# Revit family: ВИРС-М фланцевый DN15-200, PN25
name_source: partatom
category: Арматура трубопроводов
revit_build: Autodesk Revit 2015 (Build: 20140322_1515(x64)
units: mm (PartAtom-declared; Revit-internal decimal feet)

## types (88) — shared parameters
URL = http://vogez.by
Видимость клапана = Да
Диаметр подключение провода = 15 мм
Диаметр штока = 30 мм
Длина привода = 115 мм
Длина присоединения провода = 15 мм
Изготовитель = ООО "ВОГЕЗЭНЕРГО"
Интерфес (основной) = RS 232
Исполнение PN = 2
Материал и цвет ППР = Сталь, белый
Материал и цвет остальных элементов = Сталь, неокрашенная
Материал и цвет привода ППР = Пластик, серый
Наименование = Счётчик-расходомер электромагнитный
Номинальное давление PN = 2.5 МПа
Расстояние до провода = 30 мм
Скругления привода = 20 мм
Ширина привода = 65 мм

## per-type parameters (varying)
- Счётчик-расходомер электромагнитный (фланцевый) ВИРС-М DN15, PN25, серия 1000: DN=15 мм; Высота основания привода=80 мм; Высота с приводом=120 мм; Выходной сигнал=числоимпульсный; Диаметр зеркала=51 мм; Диаметр зеркала_2=21 мм; Диаметр корпуса=60 мм; Диаметр патрубка=35 мм; Диаметр условный DN=15 мм; Диаметр фланца=100 мм; Длина корпуса=72 мм; Длина по фланцам=120 мм; Исполнение=1; Класс точности=2; Максимальная температура среды=150 °C; Максимальный расход=5.0 м³/ч; Масса=3.10 kg; Минимальный расход=0.0 м³/ч; Обозначение=ВИРС-М-15-Ф-25-55-232-1000-200; Потребляемая мощность=5 Вт; Радиус условный=8 мм; Радиус фланца=50 мм; Серия=1000; Степень защиты=IP55; Строительная высота=170 мм; Строительная длина=150 мм; Тип, марка=ВИРС-М-15-Ф-25-55-232-1000-200; Толщина зеркала=2 мм; Толщина фланца=12 мм
- Счётчик-расходомер электромагнитный (фланцевый) ВИРС-М DN15, PN25, серия 2000: DN=15 мм; Высота основания привода=80 мм; Высота с приводом=120 мм; Выходной сигнал=числоимпульсный; Диаметр зеркала=51 мм; Диаметр зеркала_2=21 мм; Диаметр корпуса=60 мм; Диаметр патрубка=35 мм; Диаметр условный DN=15 мм; Диаметр фланца=100 мм; Длина корпуса=72 мм; Длина по фланцам=120 мм; Исполнение=2; Класс точности=2; Максимальная температура среды=150 °C; Максимальный расход=6.3 м³/ч; Масса=3.10 kg; Минимальный расход=0.0 м³/ч; Обозначение=ВИРС-М-15-Ф-25-55-232-2000-200; Потребляемая мощность=5 Вт; Радиус условный=8 мм; Радиус фланца=50 мм; Серия=2000; Степень защиты=IP55; Строительная высота=170 мм; Строительная длина=150 мм; Тип, марка=ВИРС-М-15-Ф-25-55-232-2000-200; Толщина зеркала=2 мм; Толщина фланца=12 мм
- Счётчик-расходомер электромагнитный (фланцевый) ВИРС-М DN15, PN25, серия 1100: DN=15 мм; Высота основания привода=80 мм; Высота с приводом=120 мм; Выходной сигнал=числоимпульсный; Диаметр зеркала=51 мм; Диаметр зеркала_2=21 мм; Диаметр корпуса=60 мм; Диаметр патрубка=35 мм; Диаметр условный DN=15 мм; Диаметр фланца=100 мм; Длина корпуса=72 мм; Длина по фланцам=120 мм; Исполнение=3; Класс точности=1; Максимальная температура среды=150 °C; Максимальный расход=5.0 м³/ч; Масса=3.10 kg; Минимальный расход=0.0 м³/ч; Обозначение=ВИРС-М-15-Ф-25-55-232-1100-100; Потребляемая мощность=5 Вт; Радиус условный=8 мм; Радиус фланца=50 мм; Серия=1100; Степень защиты=IP55; Строительная высота=170 мм; Строительная длина=150 мм; Тип, марка=ВИРС-М-15-Ф-25-55-232-1100-100; Толщина зеркала=2 мм; Толщина фланца=12 мм
- Счётчик-расходомер электромагнитный (фланцевый) ВИРС-М DN15, PN25, серия 2100: DN=15 мм; Высота основания привода=80 мм; Высота с приводом=120 мм; Выходной сигнал=числоимпульсный; Диаметр зеркала=51 мм; Диаметр зеркала_2=21 мм; Диаметр корпуса=60 мм; Диаметр патрубка=35 мм; Диаметр условный DN=15 мм; Диаметр фланца=100 мм; Длина корпуса=72 мм; Длина по фланцам=120 мм; Исполнение=4; Класс точности=1; Максимальная температура среды=150 °C; Максимальный расход=6.3 м³/ч; Масса=3.10 kg; Минимальный расход=0.0 м³/ч; Обозначение=ВИРС-М-15-Ф-25-55-232-2100-100; Потребляемая мощность=5 Вт; Радиус условный=8 мм; Радиус фланца=50 мм; Серия=2100; Степень защиты=IP55; Строительная высота=170 мм; Строительная длина=150 мм; Тип, марка=ВИРС-М-15-Ф-25-55-232-2100-100; Толщина зеркала=2 мм; Толщина фланца=12 мм
- Счётчик-расходомер электромагнитный (фланцевый) ВИРС-М DN15, PN25, серия 1300: DN=15 мм; Высота основания привода=80 мм; Высота с приводом=120 мм; Выходной сигнал=частотный; Диаметр зеркала=51 мм; Диаметр зеркала_2=21 мм; Диаметр корпуса=60 мм; Диаметр патрубка=35 мм; Диаметр условный DN=15 мм; Диаметр фланца=100 мм; Длина корпуса=72 мм; Длина по фланцам=120 мм; Исполнение=5; Класс точности=0.5; Максимальная температура среды=90 °C; Максимальный расход=5.0 м³/ч; Масса=3.10 kg; Минимальный расход=0.1 м³/ч; Обозначение=ВИРС-М-15-Ф-25-57-232-1300-050; Потребляемая мощность=5 Вт; Радиус условный=8 мм; Радиус фланца=50 мм; Серия=1300; Степень защиты=IP57; Строительная высота=170 мм; Строительная длина=150 мм; Тип, марка=ВИРС-М-15-Ф-25-57-232-1300-050; Толщина зеркала=2 мм; Толщина фланца=12 мм
- Счётчик-расходомер электромагнитный (фланцевый) ВИРС-М DN15, PN25, серия 2300: DN=15 мм; Высота основания привода=80 мм; Высота с приводом=120 мм; Выходной сигнал=частотный; Диаметр зеркала=51 мм; Диаметр зеркала_2=21 мм; Диаметр корпуса=60 мм; Диаметр патрубка=35 мм; Диаметр условный DN=15 мм; Диаметр фланца=100 мм; Длина корпуса=72 мм; Длина по фланцам=120 мм; Исполнение=6; Класс точности=0.5; Максимальная температура среды=90 °C; Максимальный расход=6.3 м³/ч; Масса=3.10 kg; Минимальный расход=0.1 м³/ч; Обозначение=ВИРС-М-15-Ф-25-57-232-2300-050; Потребляемая мощность=5 Вт; Радиус условный=8 мм; Радиус фланца=50 мм; Серия=2300; Степень защиты=IP57; Строительная высота=170 мм; Строительная длина=150 мм; Тип, марка=ВИРС-М-15-Ф-25-57-232-2300-050; Толщина зеркала=2 мм; Толщина фланца=12 мм
- Счётчик-расходомер электромагнитный (фланцевый) ВИРС-М DN15, PN25, серия 1500: DN=15 мм; Высота основания привода=80 мм; Высота с приводом=120 мм; Выходной сигнал=частотный; Диаметр зеркала=51 мм; Диаметр зеркала_2=21 мм; Диаметр корпуса=60 мм; Диаметр патрубка=35 мм; Диаметр условный DN=15 мм; Диаметр фланца=100 мм; Длина корпуса=72 мм; Длина по фланцам=120 мм; Исполнение=7; Класс точности=0.25; Максимальная температура среды=90 °C; Максимальный расход=5.0 м³/ч; Масса=3.10 kg; Минимальный расход=0.2 м³/ч; Обозначение=ВИРС-М-15-Ф-25-57-232-1500-025; Потребляемая мощность=7 Вт; Радиус условный=8 мм; Радиус фланца=50 мм; Серия=1500; Степень защиты=IP57; Строительная высота=170 мм; Строительная длина=150 мм; Тип, марка=ВИРС-М-15-Ф-25-57-232-1500-025; Толщина зеркала=2 мм; Толщина фланца=12 мм
- Счётчик-расходомер электромагнитный (фланцевый) ВИРС-М DN15, PN25, серия 2500: DN=15 мм; Высота основания привода=80 мм; Высота с приводом=120 мм; Выходной сигнал=частотный; Диаметр зеркала=51 мм; Диаметр зеркала_2=21 мм; Диаметр корпуса=60 мм; Диаметр патрубка=35 мм; Диаметр условный DN=15 мм; Диаметр фланца=100 мм; Длина корпуса=72 мм; Длина по фланцам=120 мм; Исполнение=8; Класс точности=0.25; Максимальная температура среды=90 °C; Максимальный расход=6.3 м³/ч; Масса=3.10 kg; Минимальный расход=0.3 м³/ч; Обозначение=ВИРС-М-15-Ф-25-57-232-2500-025; Потребляемая мощность=7 Вт; Радиус условный=8 мм; Радиус фланца=50 мм; Серия=2500; Степень защиты=IP57; Строительная высота=170 мм; Строительная длина=150 мм; Тип, марка=ВИРС-М-15-Ф-25-57-232-2500-025; Толщина зеркала=2 мм; Толщина фланца=12 мм
- Счётчик-расходомер электромагнитный (фланцевый) ВИРС-М DN20, PN25, серия 1000: DN=20 мм; Высота основания привода=85 мм; Высота с приводом=125 мм; Выходной сигнал=числоимпульсный; Диаметр зеркала=60 мм; Диаметр зеркала_2=25 мм; Диаметр корпуса=70 мм; Диаметр патрубка=40 мм; Диаметр условный DN=20 мм; Диаметр фланца=110 мм; Длина корпуса=68 мм; Длина по фланцам=120 мм; Исполнение=1; Класс точности=2; Максимальная температура среды=150 °C; Максимальный расход=7.9 м³/ч; Масса=3.20 kg; Минимальный расход=0.0 м³/ч; Обозначение=ВИРС-М-20-Ф-25-55-232-1000-200; Потребляемая мощность=5 Вт; Радиус условный=10 мм; Радиус фланца=55 мм; Серия=1000; Степень защиты=IP55; Строительная высота=180 мм; Строительная длина=150 мм; Тип, марка=ВИРС-М-20-Ф-25-55-232-1000-200; Толщина зеркала=2 мм; Толщина фланца=14 мм
- Счётчик-расходомер электромагнитный (фланцевый) ВИРС-М DN20, PN25, серия 1100: DN=20 мм; Высота основания привода=85 мм; Высота с приводом=125 мм; Выходной сигнал=числоимпульсный; Диаметр зеркала=60 мм; Диаметр зеркала_2=25 мм; Диаметр корпуса=70 мм; Диаметр патрубка=40 мм; Диаметр условный DN=20 мм; Диаметр фланца=110 мм; Длина корпуса=68 мм; Длина по фланцам=120 мм; Исполнение=3; Класс точности=1; Максимальная температура среды=150 °C; Максимальный расход=7.9 м³/ч; Масса=3.20 kg; Минимальный расход=0.0 м³/ч; Обозначение=ВИРС-М-20-Ф-25-55-232-1100-100; Потребляемая мощность=5 Вт; Радиус условный=10 мм; Радиус фланца=55 мм; Серия=1100; Степень защиты=IP55; Строительная высота=180 мм; Строительная длина=150 мм; Тип, марка=ВИРС-М-20-Ф-25-55-232-1100-100; Толщина зеркала=2 мм; Толщина фланца=14 мм
- Счётчик-расходомер электромагнитный (фланцевый) ВИРС-М DN20, PN25, серия 1300: DN=20 мм; Высота основания привода=85 мм; Высота с приводом=125 мм; Выходной сигнал=частотный; Диаметр зеркала=60 мм; Диаметр зеркала_2=25 мм; Диаметр корпуса=70 мм; Диаметр патрубка=40 мм; Диаметр условный DN=20 мм; Диаметр фланца=110 мм; Длина корпуса=68 мм; Длина по фланцам=120 мм; Исполнение=5; Класс точности=0.5; Максимальная температура среды=90 °C; Максимальный расход=7.9 м³/ч; Масса=3.20 kg; Минимальный расход=0.1 м³/ч; Обозначение=ВИРС-М-20-Ф-25-57-232-1300-050; Потребляемая мощность=5 Вт; Радиус условный=10 мм; Радиус фланца=55 мм; Серия=1300; Степень защиты=IP57; Строительная высота=180 мм; Строительная длина=150 мм; Тип, марка=ВИРС-М-20-Ф-25-57-232-1300-050; Толщина зеркала=2 мм; Толщина фланца=14 мм
- Счётчик-расходомер электромагнитный (фланцевый) ВИРС-М DN20, PN25, серия 1500: DN=20 мм; Высота основания привода=85 мм; Высота с приводом=125 мм; Выходной сигнал=частотный; Диаметр зеркала=60 мм; Диаметр зеркала_2=25 мм; Диаметр корпуса=70 мм; Диаметр патрубка=40 мм; Диаметр условный DN=20 мм; Диаметр фланца=110 мм; Длина корпуса=68 мм; Длина по фланцам=120 мм; Исполнение=7; Класс точности=0.25; Максимальная температура среды=90 °C; Максимальный расход=7.9 м³/ч; Масса=3.20 kg; Минимальный расход=0.3 м³/ч; Обозначение=ВИРС-М-20-Ф-25-57-232-1500-025; Потребляемая мощность=7 Вт; Радиус условный=10 мм; Радиус фланца=55 мм; Серия=1500; Степень защиты=IP57; Строительная высота=180 мм; Строительная длина=150 мм; Тип, марка=ВИРС-М-20-Ф-25-57-232-1500-025; Толщина зеркала=2 мм; Толщина фланца=14 мм
- Счётчик-расходомер электромагнитный (фланцевый) ВИРС-М DN20, PN25, серия 2000: DN=20 мм; Высота основания привода=85 мм; Высота с приводом=125 мм; Выходной сигнал=числоимпульсный; Диаметр зеркала=60 мм; Диаметр зеркала_2=25 мм; Диаметр корпуса=70 мм; Диаметр патрубка=40 мм; Диаметр условный DN=20 мм; Диаметр фланца=110 мм; Длина корпуса=68 мм; Длина по фланцам=120 мм; Исполнение=2; Класс точности=2; Максимальная температура среды=150 °C; Максимальный расход=10.0 м³/ч; Масса=3.20 kg; Минимальный расход=0.0 м³/ч; Обозначение=ВИРС-М-20-Ф-25-55-232-2000-200; Потребляемая мощность=5 Вт; Радиус условный=10 мм; Радиус фланца=55 мм; Серия=2000; Степень защиты=IP55; Строительная высота=180 мм; Строительная длина=150 мм; Тип, марка=ВИРС-М-20-Ф-25-55-232-2000-200; Толщина зеркала=2 мм; Толщина фланца=14 мм
- Счётчик-расходомер электромагнитный (фланцевый) ВИРС-М DN20, PN25, серия 2100: DN=20 мм; Высота основания привода=85 мм; Высота с приводом=125 мм; Выходной сигнал=числоимпульсный; Диаметр зеркала=60 мм; Диаметр зеркала_2=25 мм; Диаметр корпуса=70 мм; Диаметр патрубка=40 мм; Диаметр условный DN=20 мм; Диаметр фланца=110 мм; Длина корпуса=68 мм; Длина по фланцам=120 мм; Исполнение=4; Класс точности=1; Максимальная температура среды=150 °C; Максимальный расход=10.0 м³/ч; Масса=3.20 kg; Минимальный расход=0.0 м³/ч; Обозначение=ВИРС-М-20-Ф-25-55-232-2100-100; Потребляемая мощность=5 Вт; Радиус условный=10 мм; Радиус фланца=55 мм; Серия=2100; Степень защиты=IP55; Строительная высота=180 мм; Строительная длина=150 мм; Тип, марка=ВИРС-М-20-Ф-25-55-232-2100-100; Толщина зеркала=2 мм; Толщина фланца=14 мм
- Счётчик-расходомер электромагнитный (фланцевый) ВИРС-М DN20, PN25, серия 2300: DN=20 мм; Высота основания привода=85 мм; Высота с приводом=125 мм; Выходной сигнал=частотный; Диаметр зеркала=60 мм; Диаметр зеркала_2=25 мм; Диаметр корпуса=70 мм; Диаметр патрубка=40 мм; Диаметр условный DN=20 мм; Диаметр фланца=110 мм; Длина корпуса=68 мм; Длина по фланцам=120 мм; Исполнение=6; Класс точности=0.5; Максимальная температура среды=90 °C; Максимальный расход=10.0 м³/ч; Масса=3.20 kg; Минимальный расход=0.1 м³/ч; Обозначение=ВИРС-М-20-Ф-25-57-232-2300-050; Потребляемая мощность=5 Вт; Радиус условный=10 мм; Радиус фланца=55 мм; Серия=2300; Степень защиты=IP57; Строительная высота=180 мм; Строительная длина=150 мм; Тип, марка=ВИРС-М-20-Ф-25-57-232-2300-050; Толщина зеркала=2 мм; Толщина фланца=14 мм
- Счётчик-расходомер электромагнитный (фланцевый) ВИРС-М DN20, PN25, серия 2500: DN=20 мм; Высота основания привода=85 мм; Высота с приводом=125 мм; Выходной сигнал=частотный; Диаметр зеркала=60 мм; Диаметр зеркала_2=25 мм; Диаметр корпуса=70 мм; Диаметр патрубка=40 мм; Диаметр условный DN=20 мм; Диаметр фланца=110 мм; Длина корпуса=68 мм; Длина по фланцам=120 мм; Исполнение=8; Класс точности=0.25; Максимальная температура среды=90 °C; Максимальный расход=10.0 м³/ч; Масса=3.20 kg; Минимальный расход=0.4 м³/ч; Обозначение=ВИРС-М-20-Ф-25-57-232-2500-025; Потребляемая мощность=7 Вт; Радиус условный=10 мм; Радиус фланца=55 мм; Серия=2500; Степень защиты=IP57; Строительная высота=180 мм; Строительная длина=150 мм; Тип, марка=ВИРС-М-20-Ф-25-57-232-2500-025; Толщина зеркала=2 мм; Толщина фланца=14 мм
- Счётчик-расходомер электромагнитный (фланцевый) ВИРС-М DN25, PN25, серия 1000: DN=25 мм; Высота основания привода=90 мм; Высота с приводом=130 мм; Выходной сигнал=числоимпульсный; Диаметр зеркала=71 мм; Диаметр зеркала_2=31 мм; Диаметр корпуса=80 мм; Диаметр патрубка=45 мм; Диаметр условный DN=25 мм; Диаметр фланца=120 мм; Длина корпуса=64 мм; Длина по фланцам=120 мм; Исполнение=1; Класс точности=2; Максимальная температура среды=150 °C; Максимальный расход=12.5 м³/ч; Масса=3.60 kg; Минимальный расход=0.0 м³/ч; Обозначение=ВИРС-М-25-Ф-25-55-232-1000-200; Потребляемая мощность=5 Вт; Радиус условный=13 мм; Радиус фланца=60 мм; Серия=1000; Степень защиты=IP55; Строительная высота=190 мм; Строительная длина=150 мм; Тип, марка=ВИРС-М-25-Ф-25-55-232-1000-200; Толщина зеркала=2 мм; Толщина фланца=16 мм
- Счётчик-расходомер электромагнитный (фланцевый) ВИРС-М DN25, PN25, серия 1100: DN=25 мм; Высота основания привода=90 мм; Высота с приводом=130 мм; Выходной сигнал=числоимпульсный; Диаметр зеркала=71 мм; Диаметр зеркала_2=31 мм; Диаметр корпуса=80 мм; Диаметр патрубка=45 мм; Диаметр условный DN=25 мм; Диаметр фланца=120 мм; Длина корпуса=64 мм; Длина по фланцам=120 мм; Исполнение=3; Класс точности=1; Максимальная температура среды=150 °C; Максимальный расход=12.5 м³/ч; Масса=3.60 kg; Минимальный расход=0.1 м³/ч; Обозначение=ВИРС-М-25-Ф-25-55-232-1100-100; Потребляемая мощность=5 Вт; Радиус условный=13 мм; Радиус фланца=60 мм; Серия=1100; Степень защиты=IP55; Строительная высота=190 мм; Строительная длина=150 мм; Тип, марка=ВИРС-М-25-Ф-25-55-232-1100-100; Толщина зеркала=2 мм; Толщина фланца=16 мм
- Счётчик-расходомер электромагнитный (фланцевый) ВИРС-М DN25, PN25, серия 1300: DN=25 мм; Высота основания привода=90 мм; Высота с приводом=130 мм; Выходной сигнал=частотный; Диаметр зеркала=71 мм; Диаметр зеркала_2=31 мм; Диаметр корпуса=80 мм; Диаметр патрубка=45 мм; Диаметр условный DN=25 мм; Диаметр фланца=120 мм; Длина корпуса=64 мм; Длина по фланцам=120 мм; Исполнение=5; Класс точности=0.5; Максимальная температура среды=90 °C; Максимальный расход=12.5 м³/ч; Масса=3.60 kg; Минимальный расход=0.1 м³/ч; Обозначение=ВИРС-М-25-Ф-25-57-232-1300-050; Потребляемая мощность=5 Вт; Радиус условный=13 мм; Радиус фланца=60 мм; Серия=1300; Степень защиты=IP57; Строительная высота=190 мм; Строительная длина=150 мм; Тип, марка=ВИРС-М-25-Ф-25-57-232-1300-050; Толщина зеркала=2 мм; Толщина фланца=16 мм
- Счётчик-расходомер электромагнитный (фланцевый) ВИРС-М DN25, PN25, серия 1500: DN=25 мм; Высота основания привода=90 мм; Высота с приводом=130 мм; Выходной сигнал=частотный; Диаметр зеркала=71 мм; Диаметр зеркала_2=31 мм; Диаметр корпуса=80 мм; Диаметр патрубка=45 мм; Диаметр условный DN=25 мм; Диаметр фланца=120 мм; Длина корпуса=64 мм; Длина по фланцам=120 мм; Исполнение=7; Класс точности=0.25; Максимальная температура среды=90 °C; Максимальный расход=12.5 м³/ч; Масса=3.60 kg; Минимальный расход=0.5 м³/ч; Обозначение=ВИРС-М-25-Ф-25-57-232-1500-025; Потребляемая мощность=7 Вт; Радиус условный=13 мм; Радиус фланца=60 мм; Серия=1500; Степень защиты=IP57; Строительная высота=190 мм; Строительная длина=150 мм; Тип, марка=ВИРС-М-25-Ф-25-57-232-1500-025; Толщина зеркала=2 мм; Толщина фланца=16 мм
- Счётчик-расходомер электромагнитный (фланцевый) ВИРС-М DN25, PN25, серия 2000: DN=25 мм; Высота основания привода=90 мм; Высота с приводом=130 мм; Выходной сигнал=числоимпульсный; Диаметр зеркала=71 мм; Диаметр зеркала_2=31 мм; Диаметр корпуса=80 мм; Диаметр патрубка=45 мм; Диаметр условный DN=25 мм; Диаметр фланца=120 мм; Длина корпуса=64 мм; Длина по фланцам=120 мм; Исполнение=2; Класс точности=2; Максимальная температура среды=150 °C; Максимальный расход=16.0 м³/ч; Масса=3.60 kg; Минимальный расход=0.0 м³/ч; Обозначение=ВИРС-М-25-Ф-25-55-232-2000-200; Потребляемая мощность=5 Вт; Радиус условный=13 мм; Радиус фланца=60 мм; Серия=2000; Степень защиты=IP55; Строительная высота=190 мм; Строительная длина=150 мм; Тип, марка=ВИРС-М-25-Ф-25-55-232-2000-200; Толщина зеркала=2 мм; Толщина фланца=16 мм
- Счётчик-расходомер электромагнитный (фланцевый) ВИРС-М DN25, PN25, серия 2100: DN=25 мм; Высота основания привода=90 мм; Высота с приводом=130 мм; Выходной сигнал=числоимпульсный; Диаметр зеркала=71 мм; Диаметр зеркала_2=31 мм; Диаметр корпуса=80 мм; Диаметр патрубка=45 мм; Диаметр условный DN=25 мм; Диаметр фланца=120 мм; Длина корпуса=64 мм; Длина по фланцам=120 мм; Исполнение=4; Класс точности=1; Максимальная температура среды=150 °C; Максимальный расход=16.0 м³/ч; Масса=3.60 kg; Минимальный расход=0.1 м³/ч; Обозначение=ВИРС-М-25-Ф-25-55-232-2100-100; Потребляемая мощность=5 Вт; Радиус условный=13 мм; Радиус фланца=60 мм; Серия=2100; Степень защиты=IP55; Строительная высота=190 мм; Строительная длина=150 мм; Тип, марка=ВИРС-М-25-Ф-25-55-232-2100-100; Толщина зеркала=2 мм; Толщина фланца=16 мм
- Счётчик-расходомер электромагнитный (фланцевый) ВИРС-М DN25, PN25, серия 2300: DN=25 мм; Высота основания привода=90 мм; Высота с приводом=130 мм; Выходной сигнал=частотный; Диаметр зеркала=71 мм; Диаметр зеркала_2=31 мм; Диаметр корпуса=80 мм; Диаметр патрубка=45 мм; Диаметр условный DN=25 мм; Диаметр фланца=120 мм; Длина корпуса=64 мм; Длина по фланцам=120 мм; Исполнение=6; Класс точности=0.5; Максимальная температура среды=90 °C; Максимальный расход=16.0 м³/ч; Масса=3.60 kg; Минимальный расход=0.2 м³/ч; Обозначение=ВИРС-М-25-Ф-25-57-232-2300-050; Потребляемая мощность=5 Вт; Радиус условный=13 мм; Радиус фланца=60 мм; Серия=2300; Степень защиты=IP57; Строительная высота=190 мм; Строительная длина=150 мм; Тип, марка=ВИРС-М-25-Ф-25-57-232-2300-050; Толщина зеркала=2 мм; Толщина фланца=16 мм
- Счётчик-расходомер электромагнитный (фланцевый) ВИРС-М DN25, PN25, серия 2500: DN=25 мм; Высота основания привода=90 мм; Высота с приводом=130 мм; Выходной сигнал=частотный; Диаметр зеркала=71 мм; Диаметр зеркала_2=31 мм; Диаметр корпуса=80 мм; Диаметр патрубка=45 мм; Диаметр условный DN=25 мм; Диаметр фланца=120 мм; Длина корпуса=64 мм; Длина по фланцам=120 мм; Исполнение=8; Класс точности=0.25; Максимальная температура среды=90 °C; Максимальный расход=16.0 м³/ч; Масса=3.60 kg; Минимальный расход=0.6 м³/ч; Обозначение=ВИРС-М-25-Ф-25-57-232-2500-025; Потребляемая мощность=7 Вт; Радиус условный=13 мм; Радиус фланца=60 мм; Серия=2500; Степень защиты=IP57; Строительная высота=190 мм; Строительная длина=150 мм; Тип, марка=ВИРС-М-25-Ф-25-57-232-2500-025; Толщина зеркала=2 мм; Толщина фланца=16 мм
- Счётчик-расходомер электромагнитный (фланцевый) ВИРС-М DN32, PN25, серия 1000: DN=32 мм; Высота основания привода=103 мм; Высота с приводом=143 мм; Выходной сигнал=числоимпульсный; Диаметр зеркала=82 мм; Диаметр зеркала_2=36 мм; Диаметр корпуса=95 мм; Диаметр патрубка=52 мм; Диаметр условный DN=32 мм; Диаметр фланца=135 мм; Длина корпуса=114 мм; Длина по фланцам=170 мм; Исполнение=1; Класс точности=2; Максимальная температура среды=150 °C; Максимальный расход=20.0 м³/ч; Масса=4.20 kg; Минимальный расход=0.0 м³/ч; Обозначение=ВИРС-М-32-Ф-25-55-232-1000-200; Потребляемая мощность=5 Вт; Радиус условный=16 мм; Радиус фланца=68 мм; Серия=1000; Степень защиты=IP55; Строительная высота=210 мм; Строительная длина=200 мм; Тип, марка=ВИРС-М-32-Ф-25-55-232-1000-200; Толщина зеркала=2 мм; Толщина фланца=16 мм
- Счётчик-расходомер электромагнитный (фланцевый) ВИРС-М DN32, PN25, серия 1100: DN=32 мм; Высота основания привода=103 мм; Высота с приводом=143 мм; Выходной сигнал=числоимпульсный; Диаметр зеркала=82 мм; Диаметр зеркала_2=36 мм; Диаметр корпуса=95 мм; Диаметр патрубка=52 мм; Диаметр условный DN=32 мм; Диаметр фланца=135 мм; Длина корпуса=114 мм; Длина по фланцам=170 мм; Исполнение=3; Класс точности=1; Максимальная температура среды=150 °C; Максимальный расход=20.0 м³/ч; Масса=4.20 kg; Минимальный расход=0.1 м³/ч; Обозначение=ВИРС-М-32-Ф-25-55-232-1100-100; Потребляемая мощность=5 Вт; Радиус условный=16 мм; Радиус фланца=68 мм; Серия=1100; Степень защиты=IP55; Строительная высота=210 мм; Строительная длина=200 мм; Тип, марка=ВИРС-М-32-Ф-25-55-232-1100-100; Толщина зеркала=2 мм; Толщина фланца=16 мм
- Счётчик-расходомер электромагнитный (фланцевый) ВИРС-М DN32, PN25, серия 1300: DN=32 мм; Высота основания привода=103 мм; Высота с приводом=143 мм; Выходной сигнал=частотный; Диаметр зеркала=82 мм; Диаметр зеркала_2=36 мм; Диаметр корпуса=95 мм; Диаметр патрубка=52 мм; Диаметр условный DN=32 мм; Диаметр фланца=135 мм; Длина корпуса=114 мм; Длина по фланцам=170 мм; Исполнение=5; Класс точности=0.5; Максимальная температура среды=90 °C; Максимальный расход=20.0 м³/ч; Масса=4.20 kg; Минимальный расход=0.2 м³/ч; Обозначение=ВИРС-М-32-Ф-25-57-232-1300-050; Потребляемая мощность=5 Вт; Радиус условный=16 мм; Радиус фланца=68 мм; Серия=1300; Степень защиты=IP57; Строительная высота=210 мм; Строительная длина=200 мм; Тип, марка=ВИРС-М-32-Ф-25-57-232-1300-050; Толщина зеркала=2 мм; Толщина фланца=16 мм
- Счётчик-расходомер электромагнитный (фланцевый) ВИРС-М DN32, PN25, серия 1500: DN=32 мм; Высота основания привода=103 мм; Высота с приводом=143 мм; Выходной сигнал=частотный; Диаметр зеркала=82 мм; Диаметр зеркала_2=36 мм; Диаметр корпуса=95 мм; Диаметр патрубка=52 мм; Диаметр условный DN=32 мм; Диаметр фланца=135 мм; Длина корпуса=114 мм; Длина по фланцам=170 мм; Исполнение=7; Класс точности=0.25; Максимальная температура среды=90 °C; Максимальный расход=20.0 м³/ч; Масса=4.20 kg; Минимальный расход=0.8 м³/ч; Обозначение=ВИРС-М-32-Ф-25-57-232-1500-025; Потребляемая мощность=7 Вт; Радиус условный=16 мм; Радиус фланца=68 мм; Серия=1500; Степень защиты=IP57; Строительная высота=210 мм; Строительная длина=200 мм; Тип, марка=ВИРС-М-32-Ф-25-57-232-1500-025; Толщина зеркала=2 мм; Толщина фланца=16 мм
- Счётчик-расходомер электромагнитный (фланцевый) ВИРС-М DN32, PN25, серия 2000: DN=32 мм; Высота основания привода=103 мм; Высота с приводом=143 мм; Выходной сигнал=числоимпульсный; Диаметр зеркала=82 мм; Диаметр зеркала_2=36 мм; Диаметр корпуса=95 мм; Диаметр патрубка=52 мм; Диаметр условный DN=32 мм; Диаметр фланца=135 мм; Длина корпуса=114 мм; Длина по фланцам=170 мм; Исполнение=2; Класс точности=2; Максимальная температура среды=150 °C; Максимальный расход=25.0 м³/ч; Масса=4.20 kg; Минимальный расход=0.1 м³/ч; Обозначение=ВИРС-М-32-Ф-25-55-232-2000-200; Потребляемая мощность=5 Вт; Радиус условный=16 мм; Радиус фланца=68 мм; Серия=2000; Степень защиты=IP55; Строительная высота=210 мм; Строительная длина=200 мм; Тип, марка=ВИРС-М-32-Ф-25-55-232-2000-200; Толщина зеркала=2 мм; Толщина фланца=16 мм
- Счётчик-расходомер электромагнитный (фланцевый) ВИРС-М DN32, PN25, серия 2100: DN=32 мм; Высота основания привода=103 мм; Высота с приводом=143 мм; Выходной сигнал=числоимпульсный; Диаметр зеркала=82 мм; Диаметр зеркала_2=36 мм; Диаметр корпуса=95 мм; Диаметр патрубка=52 мм; Диаметр условный DN=32 мм; Диаметр фланца=135 мм; Длина корпуса=114 мм; Длина по фланцам=170 мм; Исполнение=4; Класс точности=1; Максимальная температура среды=150 °C; Максимальный расход=25.0 м³/ч; Масса=4.20 kg; Минимальный расход=0.1 м³/ч; Обозначение=ВИРС-М-32-Ф-25-55-232-2100-100; Потребляемая мощность=5 Вт; Радиус условный=16 мм; Радиус фланца=68 мм; Серия=2100; Степень защиты=IP55; Строительная высота=210 мм; Строительная длина=200 мм; Тип, марка=ВИРС-М-32-Ф-25-55-232-2100-100; Толщина зеркала=2 мм; Толщина фланца=16 мм
- Счётчик-расходомер электромагнитный (фланцевый) ВИРС-М DN32, PN25, серия 2300: DN=32 мм; Высота основания привода=103 мм; Высота с приводом=143 мм; Выходной сигнал=частотный; Диаметр зеркала=82 мм; Диаметр зеркала_2=36 мм; Диаметр корпуса=95 мм; Диаметр патрубка=52 мм; Диаметр условный DN=32 мм; Диаметр фланца=135 мм; Длина корпуса=114 мм; Длина по фланцам=170 мм; Исполнение=6; Класс точности=0.5; Максимальная температура среды=90 °C; Максимальный расход=25.0 м³/ч; Масса=4.20 kg; Минимальный расход=0.3 м³/ч; Обозначение=ВИРС-М-32-Ф-25-57-232-2300-050; Потребляемая мощность=5 Вт; Радиус условный=16 мм; Радиус фланца=68 мм; Серия=2300; Степень защиты=IP57; Строительная высота=210 мм; Строительная длина=200 мм; Тип, марка=ВИРС-М-32-Ф-25-57-232-2300-050; Толщина зеркала=2 мм; Толщина фланца=16 мм
- Счётчик-расходомер электромагнитный (фланцевый) ВИРС-М DN32, PN25, серия 2500: DN=32 мм; Высота основания привода=103 мм; Высота с приводом=143 мм; Выходной сигнал=частотный; Диаметр зеркала=82 мм; Диаметр зеркала_2=36 мм; Диаметр корпуса=95 мм; Диаметр патрубка=52 мм; Диаметр условный DN=32 мм; Диаметр фланца=135 мм; Длина корпуса=114 мм; Длина по фланцам=170 мм; Исполнение=8; Класс точности=0.25; Максимальная температура среды=90 °C; Максимальный расход=25.0 м³/ч; Масса=4.20 kg; Минимальный расход=1.0 м³/ч; Обозначение=ВИРС-М-32-Ф-25-57-232-2500-025; Потребляемая мощность=7 Вт; Радиус условный=16 мм; Радиус фланца=68 мм; Серия=2500; Степень защиты=IP57; Строительная высота=210 мм; Строительная длина=200 мм; Тип, марка=ВИРС-М-32-Ф-25-57-232-2500-025; Толщина зеркала=2 мм; Толщина фланца=16 мм
- Счётчик-расходомер электромагнитный (фланцевый) ВИРС-М DN40, PN25, серия 1000: DN=40 мм; Высота основания привода=108 мм; Высота с приводом=148 мм; Выходной сигнал=числоимпульсный; Диаметр зеркала=92 мм; Диаметр зеркала_2=41 мм; Диаметр корпуса=105 мм; Диаметр патрубка=60 мм; Диаметр условный DN=40 мм; Диаметр фланца=145 мм; Длина корпуса=110 мм; Длина по фланцам=170 мм; Исполнение=1; Класс точности=2; Максимальная температура среды=150 °C; Максимальный расход=31.3 м³/ч; Масса=5.30 kg; Минимальный расход=0.1 м³/ч; Обозначение=ВИРС-М-40-Ф-25-55-232-1000-200; Потребляемая мощность=5 Вт; Радиус условный=20 мм; Радиус фланца=73 мм; Серия=1000; Степень защиты=IP55; Строительная высота=220 мм; Строительная длина=200 мм; Тип, марка=ВИРС-М-40-Ф-25-55-232-1000-200; Толщина зеркала=3 мм; Толщина фланца=17 мм
- Счётчик-расходомер электромагнитный (фланцевый) ВИРС-М DN40, PN25, серия 1100: DN=40 мм; Высота основания привода=108 мм; Высота с приводом=148 мм; Выходной сигнал=числоимпульсный; Диаметр зеркала=92 мм; Диаметр зеркала_2=41 мм; Диаметр корпуса=105 мм; Диаметр патрубка=60 мм; Диаметр условный DN=40 мм; Диаметр фланца=145 мм; Длина корпуса=110 мм; Длина по фланцам=170 мм; Исполнение=3; Класс точности=1; Максимальная температура среды=150 °C; Максимальный расход=31.3 м³/ч; Масса=5.30 kg; Минимальный расход=0.1 м³/ч; Обозначение=ВИРС-М-40-Ф-25-55-232-1100-100; Потребляемая мощность=5 Вт; Радиус условный=20 мм; Радиус фланца=73 мм; Серия=1100; Степень защиты=IP55; Строительная высота=220 мм; Строительная длина=200 мм; Тип, марка=ВИРС-М-40-Ф-25-55-232-1100-100; Толщина зеркала=3 мм; Толщина фланца=17 мм
- Счётчик-расходомер электромагнитный (фланцевый) ВИРС-М DN40, PN25, серия 1300: DN=40 мм; Высота основания привода=108 мм; Высота с приводом=148 мм; Выходной сигнал=частотный; Диаметр зеркала=92 мм; Диаметр зеркала_2=41 мм; Диаметр корпуса=105 мм; Диаметр патрубка=60 мм; Диаметр условный DN=40 мм; Диаметр фланца=145 мм; Длина корпуса=110 мм; Длина по фланцам=170 мм; Исполнение=5; Класс точности=0.5; Максимальная температура среды=90 °C; Максимальный расход=31.3 м³/ч; Масса=5.30 kg; Минимальный расход=0.3 м³/ч; Обозначение=ВИРС-М-40-Ф-25-57-232-1300-050; Потребляемая мощность=5 Вт; Радиус условный=20 мм; Радиус фланца=73 мм; Серия=1300; Степень защиты=IP57; Строительная высота=220 мм; Строительная длина=200 мм; Тип, марка=ВИРС-М-40-Ф-25-57-232-1300-050; Толщина зеркала=3 мм; Толщина фланца=17 мм
- Счётчик-расходомер электромагнитный (фланцевый) ВИРС-М DN40, PN25, серия 1500: DN=40 мм; Высота основания привода=108 мм; Высота с приводом=148 мм; Выходной сигнал=частотный; Диаметр зеркала=92 мм; Диаметр зеркала_2=41 мм; Диаметр корпуса=105 мм; Диаметр патрубка=60 мм; Диаметр условный DN=40 мм; Диаметр фланца=145 мм; Длина корпуса=110 мм; Длина по фланцам=170 мм; Исполнение=7; Класс точности=0.25; Максимальная температура среды=90 °C; Максимальный расход=31.3 м³/ч; Масса=5.30 kg; Минимальный расход=1.3 м³/ч; Обозначение=ВИРС-М-40-Ф-25-57-232-1500-025; Потребляемая мощность=7 Вт; Радиус условный=20 мм; Радиус фланца=73 мм; Серия=1500; Степень защиты=IP57; Строительная высота=220 мм; Строительная длина=200 мм; Тип, марка=ВИРС-М-40-Ф-25-57-232-1500-025; Толщина зеркала=3 мм; Толщина фланца=17 мм
- Счётчик-расходомер электромагнитный (фланцевый) ВИРС-М DN40, PN25, серия 2000: DN=40 мм; Высота основания привода=108 мм; Высота с приводом=148 мм; Выходной сигнал=числоимпульсный; Диаметр зеркала=92 мм; Диаметр зеркала_2=41 мм; Диаметр корпуса=105 мм; Диаметр патрубка=60 мм; Диаметр условный DN=40 мм; Диаметр фланца=145 мм; Длина корпуса=110 мм; Длина по фланцам=170 мм; Исполнение=2; Класс точности=2; Максимальная температура среды=150 °C; Максимальный расход=40.0 м³/ч; Масса=5.30 kg; Минимальный расход=0.1 м³/ч; Обозначение=ВИРС-М-40-Ф-25-55-232-2000-200; Потребляемая мощность=5 Вт; Радиус условный=20 мм; Радиус фланца=73 мм; Серия=2000; Степень защиты=IP55; Строительная высота=220 мм; Строительная длина=200 мм; Тип, марка=ВИРС-М-40-Ф-25-55-232-2000-200; Толщина зеркала=3 мм; Толщина фланца=17 мм
- Счётчик-расходомер электромагнитный (фланцевый) ВИРС-М DN40, PN25, серия 2100: DN=40 мм; Высота основания привода=108 мм; Высота с приводом=148 мм; Выходной сигнал=числоимпульсный; Диаметр зеркала=92 мм; Диаметр зеркала_2=41 мм; Диаметр корпуса=105 мм; Диаметр патрубка=60 мм; Диаметр условный DN=40 мм; Диаметр фланца=145 мм; Длина корпуса=110 мм; Длина по фланцам=170 мм; Исполнение=4; Класс точности=1; Максимальная температура среды=150 °C; Максимальный расход=40.0 м³/ч; Масса=5.30 kg; Минимальный расход=0.2 м³/ч; Обозначение=ВИРС-М-40-Ф-25-55-232-2100-100; Потребляемая мощность=5 Вт; Радиус условный=20 мм; Радиус фланца=73 мм; Серия=2100; Степень защиты=IP55; Строительная высота=220 мм; Строительная длина=200 мм; Тип, марка=ВИРС-М-40-Ф-25-55-232-2100-100; Толщина зеркала=3 мм; Толщина фланца=17 мм
- Счётчик-расходомер электромагнитный (фланцевый) ВИРС-М DN40, PN25, серия 2300: DN=40 мм; Высота основания привода=108 мм; Высота с приводом=148 мм; Выходной сигнал=частотный; Диаметр зеркала=92 мм; Диаметр зеркала_2=41 мм; Диаметр корпуса=105 мм; Диаметр патрубка=60 мм; Диаметр условный DN=40 мм; Диаметр фланца=145 мм; Длина корпуса=110 мм; Длина по фланцам=170 мм; Исполнение=6; Класс точности=0.5; Максимальная температура среды=90 °C; Максимальный расход=40.0 м³/ч; Масса=5.30 kg; Минимальный расход=0.4 м³/ч; Обозначение=ВИРС-М-40-Ф-25-57-232-2300-050; Потребляемая мощность=5 Вт; Радиус условный=20 мм; Радиус фланца=73 мм; Серия=2300; Степень защиты=IP57; Строительная высота=220 мм; Строительная длина=200 мм; Тип, марка=ВИРС-М-40-Ф-25-57-232-2300-050; Толщина зеркала=3 мм; Толщина фланца=17 мм
- Счётчик-расходомер электромагнитный (фланцевый) ВИРС-М DN40, PN25, серия 2500: DN=40 мм; Высота основания привода=108 мм; Высота с приводом=148 мм; Выходной сигнал=частотный; Диаметр зеркала=92 мм; Диаметр зеркала_2=41 мм; Диаметр корпуса=105 мм; Диаметр патрубка=60 мм; Диаметр условный DN=40 мм; Диаметр фланца=145 мм; Длина корпуса=110 мм; Длина по фланцам=170 мм; Исполнение=8; Класс точности=0.25; Максимальная температура среды=90 °C; Максимальный расход=40.0 м³/ч; Масса=5.30 kg; Минимальный расход=1.6 м³/ч; Обозначение=ВИРС-М-40-Ф-25-57-232-2500-025; Потребляемая мощность=7 Вт; Радиус условный=20 мм; Радиус фланца=73 мм; Серия=2500; Степень защиты=IP57; Строительная высота=220 мм; Строительная длина=200 мм; Тип, марка=ВИРС-М-40-Ф-25-57-232-2500-025; Толщина зеркала=3 мм; Толщина фланца=17 мм
- Счётчик-расходомер электромагнитный (фланцевый) ВИРС-М DN50, PN25, серия 1000: DN=50 мм; Высота основания привода=110 мм; Высота с приводом=150 мм; Выходной сигнал=числоимпульсный; Диаметр зеркала=107 мм; Диаметр зеркала_2=49 мм; Диаметр корпуса=120 мм; Диаметр патрубка=70 мм; Диаметр условный DN=50 мм; Диаметр фланца=160 мм; Длина корпуса=106 мм; Длина по фланцам=170 мм; Исполнение=1; Класс точности=2; Максимальная температура среды=150 °C; Максимальный расход=50.0 м³/ч; Масса=6.80 kg; Минимальный расход=0.1 м³/ч; Обозначение=ВИРС-М-50-Ф-25-55-232-1000-200; Потребляемая мощность=5 Вт; Радиус условный=25 мм; Радиус фланца=80 мм; Серия=1000; Степень защиты=IP55; Строительная высота=230 мм; Строительная длина=200 мм; Тип, марка=ВИРС-М-50-Ф-25-55-232-1000-200; Толщина зеркала=3 мм; Толщина фланца=19 мм
- Счётчик-расходомер электромагнитный (фланцевый) ВИРС-М DN50, PN25, серия 1100: DN=50 мм; Высота основания привода=110 мм; Высота с приводом=150 мм; Выходной сигнал=числоимпульсный; Диаметр зеркала=107 мм; Диаметр зеркала_2=49 мм; Диаметр корпуса=120 мм; Диаметр патрубка=70 мм; Диаметр условный DN=50 мм; Диаметр фланца=160 мм; Длина корпуса=106 мм; Длина по фланцам=170 мм; Исполнение=3; Класс точности=1; Максимальная температура среды=150 °C; Максимальный расход=50.0 м³/ч; Масса=6.80 kg; Минимальный расход=0.2 м³/ч; Обозначение=ВИРС-М-50-Ф-25-55-232-1100-100; Потребляемая мощность=5 Вт; Радиус условный=25 мм; Радиус фланца=80 мм; Серия=1100; Степень защиты=IP55; Строительная высота=230 мм; Строительная длина=200 мм; Тип, марка=ВИРС-М-50-Ф-25-55-232-1100-100; Толщина зеркала=3 мм; Толщина фланца=19 мм
- Счётчик-расходомер электромагнитный (фланцевый) ВИРС-М DN50, PN25, серия 1300: DN=50 мм; Высота основания привода=110 мм; Высота с приводом=150 мм; Выходной сигнал=частотный; Диаметр зеркала=107 мм; Диаметр зеркала_2=49 мм; Диаметр корпуса=120 мм; Диаметр патрубка=70 мм; Диаметр условный DN=50 мм; Диаметр фланца=160 мм; Длина корпуса=106 мм; Длина по фланцам=170 мм; Исполнение=5; Класс точности=0.5; Максимальная температура среды=90 °C; Максимальный расход=50.0 м³/ч; Масса=6.80 kg; Минимальный расход=0.5 м³/ч; Обозначение=ВИРС-М-50-Ф-25-57-232-1300-050; Потребляемая мощность=5 Вт; Радиус условный=25 мм; Радиус фланца=80 мм; Серия=1300; Степень защиты=IP57; Строительная высота=230 мм; Строительная длина=200 мм; Тип, марка=ВИРС-М-50-Ф-25-57-232-1300-050; Толщина зеркала=3 мм; Толщина фланца=19 мм
- Счётчик-расходомер электромагнитный (фланцевый) ВИРС-М DN50, PN25, серия 1500: DN=50 мм; Высота основания привода=110 мм; Высота с приводом=150 мм; Выходной сигнал=частотный; Диаметр зеркала=107 мм; Диаметр зеркала_2=49 мм; Диаметр корпуса=120 мм; Диаметр патрубка=70 мм; Диаметр условный DN=50 мм; Диаметр фланца=160 мм; Длина корпуса=106 мм; Длина по фланцам=170 мм; Исполнение=7; Класс точности=0.25; Максимальная температура среды=90 °C; Максимальный расход=50.0 м³/ч; Масса=6.80 kg; Минимальный расход=2.0 м³/ч; Обозначение=ВИРС-М-50-Ф-25-57-232-1500-025; Потребляемая мощность=7 Вт; Радиус условный=25 мм; Радиус фланца=80 мм; Серия=1500; Степень защиты=IP57; Строительная высота=230 мм; Строительная длина=200 мм; Тип, марка=ВИРС-М-50-Ф-25-57-232-1500-025; Толщина зеркала=3 мм; Толщина фланца=19 мм
- Счётчик-расходомер электромагнитный (фланцевый) ВИРС-М DN50, PN25, серия 2000: DN=50 мм; Высота основания привода=110 мм; Высота с приводом=150 мм; Выходной сигнал=числоимпульсный; Диаметр зеркала=107 мм; Диаметр зеркала_2=49 мм; Диаметр корпуса=120 мм; Диаметр патрубка=70 мм; Диаметр условный DN=50 мм; Диаметр фланца=160 мм; Длина корпуса=106 мм; Длина по фланцам=170 мм; Исполнение=2; Класс точности=2; Максимальная температура среды=150 °C; Максимальный расход=63.0 м³/ч; Масса=6.80 kg; Минимальный расход=0.1 м³/ч; Обозначение=ВИРС-М-50-Ф-25-55-232-2000-200; Потребляемая мощность=5 Вт; Радиус условный=25 мм; Радиус фланца=80 мм; Серия=2000; Степень защиты=IP55; Строительная высота=230 мм; Строительная длина=200 мм; Тип, марка=ВИРС-М-50-Ф-25-55-232-2000-200; Толщина зеркала=3 мм; Толщина фланца=19 мм
- Счётчик-расходомер электромагнитный (фланцевый) ВИРС-М DN50, PN25, серия 2100: DN=50 мм; Высота основания привода=110 мм; Высота с приводом=150 мм; Выходной сигнал=числоимпульсный; Диаметр зеркала=107 мм; Диаметр зеркала_2=49 мм; Диаметр корпуса=120 мм; Диаметр патрубка=70 мм; Диаметр условный DN=50 мм; Диаметр фланца=160 мм; Длина корпуса=106 мм; Длина по фланцам=170 мм; Исполнение=4; Класс точности=1; Максимальная температура среды=150 °C; Максимальный расход=63.0 м³/ч; Масса=6.80 kg; Минимальный расход=0.3 м³/ч; Обозначение=ВИРС-М-50-Ф-25-55-232-2100-100; Потребляемая мощность=5 Вт; Радиус условный=25 мм; Радиус фланца=80 мм; Серия=2100; Степень защиты=IP55; Строительная высота=230 мм; Строительная длина=200 мм; Тип, марка=ВИРС-М-50-Ф-25-55-232-2100-100; Толщина зеркала=3 мм; Толщина фланца=19 мм
- Счётчик-расходомер электромагнитный (фланцевый) ВИРС-М DN50, PN25, серия 2300: DN=50 мм; Высота основания привода=110 мм; Высота с приводом=150 мм; Выходной сигнал=частотный; Диаметр зеркала=107 мм; Диаметр зеркала_2=49 мм; Диаметр корпуса=120 мм; Диаметр патрубка=70 мм; Диаметр условный DN=50 мм; Диаметр фланца=160 мм; Длина корпуса=106 мм; Длина по фланцам=170 мм; Исполнение=6; Класс точности=0.5; Максимальная температура среды=90 °C; Максимальный расход=63.0 м³/ч; Масса=6.80 kg; Минимальный расход=0.6 м³/ч; Обозначение=ВИРС-М-50-Ф-25-57-232-2300-050; Потребляемая мощность=5 Вт; Радиус условный=25 мм; Радиус фланца=80 мм; Серия=2300; Степень защиты=IP57; Строительная высота=230 мм; Строительная длина=200 мм; Тип, марка=ВИРС-М-50-Ф-25-57-232-2300-050; Толщина зеркала=3 мм; Толщина фланца=19 мм
- Счётчик-расходомер электромагнитный (фланцевый) ВИРС-М DN50, PN25, серия 2500: DN=50 мм; Высота основания привода=110 мм; Высота с приводом=150 мм; Выходной сигнал=частотный; Диаметр зеркала=107 мм; Диаметр зеркала_2=49 мм; Диаметр корпуса=120 мм; Диаметр патрубка=70 мм; Диаметр условный DN=50 мм; Диаметр фланца=160 мм; Длина корпуса=106 мм; Длина по фланцам=170 мм; Исполнение=8; Класс точности=0.25; Максимальная температура среды=90 °C; Максимальный расход=63.0 м³/ч; Масса=6.80 kg; Минимальный расход=2.5 м³/ч; Обозначение=ВИРС-М-50-Ф-25-57-232-2500-025; Потребляемая мощность=7 Вт; Радиус условный=25 мм; Радиус фланца=80 мм; Серия=2500; Степень защиты=IP57; Строительная высота=230 мм; Строительная длина=200 мм; Тип, марка=ВИРС-М-50-Ф-25-57-232-2500-025; Толщина зеркала=3 мм; Толщина фланца=19 мм
- Счётчик-расходомер электромагнитный (фланцевый) ВИРС-М DN65, PN25, серия 1000: DN=65 мм; Высота основания привода=120 мм; Высота с приводом=160 мм; Выходной сигнал=числоимпульсный; Диаметр зеркала=127 мм; Диаметр зеркала_2=59 мм; Диаметр корпуса=140 мм; Диаметр патрубка=85 мм; Диаметр условный DN=65 мм; Диаметр фланца=180 мм; Длина корпуса=102 мм; Длина по фланцам=170 мм; Исполнение=1; Класс точности=2; Максимальная температура среды=150 °C; Максимальный расход=78.8 м³/ч; Масса=11.00 kg; Минимальный расход=0.2 м³/ч; Обозначение=ВИРС-М-65-Ф-25-55-232-1000-200; Потребляемая мощность=5 Вт; Радиус условный=33 мм; Радиус фланца=90 мм; Серия=1000; Степень защиты=IP55; Строительная высота=250 мм; Строительная длина=200 мм; Тип, марка=ВИРС-М-65-Ф-25-55-232-1000-200; Толщина зеркала=3 мм; Толщина фланца=21 мм
- Счётчик-расходомер электромагнитный (фланцевый) ВИРС-М DN65, PN25, серия 1100: DN=65 мм; Высота основания привода=120 мм; Высота с приводом=160 мм; Выходной сигнал=числоимпульсный; Диаметр зеркала=127 мм; Диаметр зеркала_2=59 мм; Диаметр корпуса=140 мм; Диаметр патрубка=85 мм; Диаметр условный DN=65 мм; Диаметр фланца=180 мм; Длина корпуса=102 мм; Длина по фланцам=170 мм; Исполнение=3; Класс точности=1; Максимальная температура среды=150 °C; Максимальный расход=78.8 м³/ч; Масса=11.00 kg; Минимальный расход=0.3 м³/ч; Обозначение=ВИРС-М-65-Ф-25-55-232-1100-100; Потребляемая мощность=5 Вт; Радиус условный=33 мм; Радиус фланца=90 мм; Серия=1100; Степень защиты=IP55; Строительная высота=250 мм; Строительная длина=200 мм; Тип, марка=ВИРС-М-65-Ф-25-55-232-1100-100; Толщина зеркала=3 мм; Толщина фланца=21 мм
- Счётчик-расходомер электромагнитный (фланцевый) ВИРС-М DN65, PN25, серия 1300: DN=65 мм; Высота основания привода=120 мм; Высота с приводом=160 мм; Выходной сигнал=частотный; Диаметр зеркала=127 мм; Диаметр зеркала_2=59 мм; Диаметр корпуса=140 мм; Диаметр патрубка=85 мм; Диаметр условный DN=65 мм; Диаметр фланца=180 мм; Длина корпуса=102 мм; Длина по фланцам=170 мм; Исполнение=5; Класс точности=0.5; Максимальная температура среды=90 °C; Максимальный расход=78.8 м³/ч; Масса=11.00 kg; Минимальный расход=0.8 м³/ч; Обозначение=ВИРС-М-65-Ф-25-57-232-1300-050; Потребляемая мощность=5 Вт; Радиус условный=33 мм; Радиус фланца=90 мм; Серия=1300; Степень защиты=IP57; Строительная высота=250 мм; Строительная длина=200 мм; Тип, марка=ВИРС-М-65-Ф-25-57-232-1300-050; Толщина зеркала=3 мм; Толщина фланца=21 мм
- Счётчик-расходомер электромагнитный (фланцевый) ВИРС-М DN65, PN25, серия 1500: DN=65 мм; Высота основания привода=120 мм; Высота с приводом=160 мм; Выходной сигнал=частотный; Диаметр зеркала=127 мм; Диаметр зеркала_2=59 мм; Диаметр корпуса=140 мм; Диаметр патрубка=85 мм; Диаметр условный DN=65 мм; Диаметр фланца=180 мм; Длина корпуса=102 мм; Длина по фланцам=170 мм; Исполнение=7; Класс точности=0.25; Максимальная температура среды=90 °C; Максимальный расход=78.8 м³/ч; Масса=11.00 kg; Минимальный расход=3.2 м³/ч; Обозначение=ВИРС-М-65-Ф-25-57-232-1500-025; Потребляемая мощность=7 Вт; Радиус условный=33 мм; Радиус фланца=90 мм; Серия=1500; Степень защиты=IP57; Строительная высота=250 мм; Строительная длина=200 мм; Тип, марка=ВИРС-М-65-Ф-25-57-232-1500-025; Толщина зеркала=3 мм; Толщина фланца=21 мм
- Счётчик-расходомер электромагнитный (фланцевый) ВИРС-М DN65, PN25, серия 2000: DN=65 мм; Высота основания привода=120 мм; Высота с приводом=160 мм; Выходной сигнал=числоимпульсный; Диаметр зеркала=127 мм; Диаметр зеркала_2=59 мм; Диаметр корпуса=140 мм; Диаметр патрубка=85 мм; Диаметр условный DN=65 мм; Диаметр фланца=180 мм; Длина корпуса=102 мм; Длина по фланцам=170 мм; Исполнение=2; Класс точности=2; Максимальная температура среды=150 °C; Максимальный расход=100.0 м³/ч; Масса=11.00 kg; Минимальный расход=0.2 м³/ч; Обозначение=ВИРС-М-65-Ф-25-55-232-2000-200; Потребляемая мощность=5 Вт; Радиус условный=33 мм; Радиус фланца=90 мм; Серия=2000; Степень защиты=IP55; Строительная высота=250 мм; Строительная длина=200 мм; Тип, марка=ВИРС-М-65-Ф-25-55-232-2000-200; Толщина зеркала=3 мм; Толщина фланца=21 мм
- Счётчик-расходомер электромагнитный (фланцевый) ВИРС-М DN65, PN25, серия 2100: DN=65 мм; Высота основания привода=120 мм; Высота с приводом=160 мм; Выходной сигнал=числоимпульсный; Диаметр зеркала=127 мм; Диаметр зеркала_2=59 мм; Диаметр корпуса=140 мм; Диаметр патрубка=85 мм; Диаметр условный DN=65 мм; Диаметр фланца=180 мм; Длина корпуса=102 мм; Длина по фланцам=170 мм; Исполнение=4; Класс точности=1; Максимальная температура среды=150 °C; Максимальный расход=100.0 м³/ч; Масса=11.00 kg; Минимальный расход=0.4 м³/ч; Обозначение=ВИРС-М-65-Ф-25-55-232-2100-100; Потребляемая мощность=5 Вт; Радиус условный=33 мм; Радиус фланца=90 мм; Серия=2100; Степень защиты=IP55; Строительная высота=250 мм; Строительная длина=200 мм; Тип, марка=ВИРС-М-65-Ф-25-55-232-2100-100; Толщина зеркала=3 мм; Толщина фланца=21 мм
- Счётчик-расходомер электромагнитный (фланцевый) ВИРС-М DN65, PN25, серия 2300: DN=65 мм; Высота основания привода=120 мм; Высота с приводом=160 мм; Выходной сигнал=частотный; Диаметр зеркала=127 мм; Диаметр зеркала_2=59 мм; Диаметр корпуса=140 мм; Диаметр патрубка=85 мм; Диаметр условный DN=65 мм; Диаметр фланца=180 мм; Длина корпуса=102 мм; Длина по фланцам=170 мм; Исполнение=6; Класс точности=0.5; Максимальная температура среды=90 °C; Максимальный расход=100.0 м³/ч; Масса=11.00 kg; Минимальный расход=1.0 м³/ч; Обозначение=ВИРС-М-65-Ф-25-57-232-2300-050; Потребляемая мощность=5 Вт; Радиус условный=33 мм; Радиус фланца=90 мм; Серия=2300; Степень защиты=IP57; Строительная высота=250 мм; Строительная длина=200 мм; Тип, марка=ВИРС-М-65-Ф-25-57-232-2300-050; Толщина зеркала=3 мм; Толщина фланца=21 мм
- Счётчик-расходомер электромагнитный (фланцевый) ВИРС-М DN65, PN25, серия 2500: DN=65 мм; Высота основания привода=120 мм; Высота с приводом=160 мм; Выходной сигнал=частотный; Диаметр зеркала=127 мм; Диаметр зеркала_2=59 мм; Диаметр корпуса=140 мм; Диаметр патрубка=85 мм; Диаметр условный DN=65 мм; Диаметр фланца=180 мм; Длина корпуса=102 мм; Длина по фланцам=170 мм; Исполнение=8; Класс точности=0.25; Максимальная температура среды=90 °C; Максимальный расход=100.0 м³/ч; Масса=11.00 kg; Минимальный расход=4.0 м³/ч; Обозначение=ВИРС-М-65-Ф-25-57-232-2500-025; Потребляемая мощность=7 Вт; Радиус условный=33 мм; Радиус фланца=90 мм; Серия=2500; Степень защиты=IP57; Строительная высота=250 мм; Строительная длина=200 мм; Тип, марка=ВИРС-М-65-Ф-25-57-232-2500-025; Толщина зеркала=3 мм; Толщина фланца=21 мм
- Счётчик-расходомер электромагнитный (фланцевый) ВИРС-М DN80, PN25, серия 1000: DN=80 мм; Высота основания привода=123 мм; Высота с приводом=163 мм; Выходной сигнал=числоимпульсный; Диаметр зеркала=139 мм; Диаметр зеркала_2=65 мм; Диаметр корпуса=155 мм; Диаметр патрубка=100 мм; Диаметр условный DN=80 мм; Диаметр фланца=195 мм; Длина корпуса=152 мм; Длина по фланцам=220 мм; Исполнение=1; Класс точности=2; Максимальная температура среды=150 °C; Максимальный расход=125.0 м³/ч; Масса=14.00 kg; Минимальный расход=0.3 м³/ч; Обозначение=ВИРС-М-80-Ф-25-55-232-1000-200; Потребляемая мощность=5 Вт; Радиус условный=40 мм; Радиус фланца=98 мм; Серия=1000; Степень защиты=IP55; Строительная высота=260 мм; Строительная длина=250 мм; Тип, марка=ВИРС-М-80-Ф-25-55-232-1000-200; Толщина зеркала=3 мм; Толщина фланца=21 мм
- Счётчик-расходомер электромагнитный (фланцевый) ВИРС-М DN80, PN25, серия 1100: DN=80 мм; Высота основания привода=123 мм; Высота с приводом=163 мм; Выходной сигнал=числоимпульсный; Диаметр зеркала=139 мм; Диаметр зеркала_2=65 мм; Диаметр корпуса=155 мм; Диаметр патрубка=100 мм; Диаметр условный DN=80 мм; Диаметр фланца=195 мм; Длина корпуса=152 мм; Длина по фланцам=220 мм; Исполнение=3; Класс точности=1; Максимальная температура среды=150 °C; Максимальный расход=125.0 м³/ч; Масса=14.00 kg; Минимальный расход=0.5 м³/ч; Обозначение=ВИРС-М-80-Ф-25-55-232-1100-100; Потребляемая мощность=5 Вт; Радиус условный=40 мм; Радиус фланца=98 мм; Серия=1100; Степень защиты=IP55; Строительная высота=260 мм; Строительная длина=250 мм; Тип, марка=ВИРС-М-80-Ф-25-55-232-1100-100; Толщина зеркала=3 мм; Толщина фланца=21 мм
- Счётчик-расходомер электромагнитный (фланцевый) ВИРС-М DN80, PN25, серия 1300: DN=80 мм; Высота основания привода=123 мм; Высота с приводом=163 мм; Выходной сигнал=частотный; Диаметр зеркала=139 мм; Диаметр зеркала_2=65 мм; Диаметр корпуса=155 мм; Диаметр патрубка=100 мм; Диаметр условный DN=80 мм; Диаметр фланца=195 мм; Длина корпуса=152 мм; Длина по фланцам=220 мм; Исполнение=5; Класс точности=0.5; Максимальная температура среды=90 °C; Максимальный расход=125.0 м³/ч; Масса=14.00 kg; Минимальный расход=1.3 м³/ч; Обозначение=ВИРС-М-80-Ф-25-57-232-1300-050; Потребляемая мощность=5 Вт; Радиус условный=40 мм; Радиус фланца=98 мм; Серия=1300; Степень защиты=IP57; Строительная высота=260 мм; Строительная длина=250 мм; Тип, марка=ВИРС-М-80-Ф-25-57-232-1300-050; Толщина зеркала=3 мм; Толщина фланца=21 мм
- Счётчик-расходомер электромагнитный (фланцевый) ВИРС-М DN80, PN25, серия 1500: DN=80 мм; Высота основания привода=123 мм; Высота с приводом=163 мм; Выходной сигнал=частотный; Диаметр зеркала=139 мм; Диаметр зеркала_2=65 мм; Диаметр корпуса=155 мм; Диаметр патрубка=100 мм; Диаметр условный DN=80 мм; Диаметр фланца=195 мм; Длина корпуса=152 мм; Длина по фланцам=220 мм; Исполнение=7; Класс точности=0.25; Максимальная температура среды=90 °C; Максимальный расход=125.0 м³/ч; Масса=14.00 kg; Минимальный расход=5.0 м³/ч; Обозначение=ВИРС-М-80-Ф-25-57-232-1500-025; Потребляемая мощность=7 Вт; Радиус условный=40 мм; Радиус фланца=98 мм; Серия=1500; Степень защиты=IP57; Строительная высота=260 мм; Строительная длина=250 мм; Тип, марка=ВИРС-М-80-Ф-25-57-232-1500-025; Толщина зеркала=3 мм; Толщина фланца=21 мм
- Счётчик-расходомер электромагнитный (фланцевый) ВИРС-М DN80, PN25, серия 2000: DN=80 мм; Высота основания привода=123 мм; Высота с приводом=163 мм; Выходной сигнал=числоимпульсный; Диаметр зеркала=139 мм; Диаметр зеркала_2=65 мм; Диаметр корпуса=155 мм; Диаметр патрубка=100 мм; Диаметр условный DN=80 мм; Диаметр фланца=195 мм; Длина корпуса=152 мм; Длина по фланцам=220 мм; Исполнение=2; Класс точности=2; Максимальная температура среды=150 °C; Максимальный расход=160.0 м³/ч; Масса=14.00 kg; Минимальный расход=0.3 м³/ч; Обозначение=ВИРС-М-80-Ф-25-55-232-2000-200; Потребляемая мощность=5 Вт; Радиус условный=40 мм; Радиус фланца=98 мм; Серия=2000; Степень защиты=IP55; Строительная высота=260 мм; Строительная длина=250 мм; Тип, марка=ВИРС-М-80-Ф-25-55-232-2000-200; Толщина зеркала=3 мм; Толщина фланца=21 мм
- Счётчик-расходомер электромагнитный (фланцевый) ВИРС-М DN80, PN25, серия 2100: DN=80 мм; Высота основания привода=123 мм; Высота с приводом=163 мм; Выходной сигнал=числоимпульсный; Диаметр зеркала=139 мм; Диаметр зеркала_2=65 мм; Диаметр корпуса=155 мм; Диаметр патрубка=100 мм; Диаметр условный DN=80 мм; Диаметр фланца=195 мм; Длина корпуса=152 мм; Длина по фланцам=220 мм; Исполнение=4; Класс точности=1; Максимальная температура среды=150 °C; Максимальный расход=160.0 м³/ч; Масса=14.00 kg; Минимальный расход=0.6 м³/ч; Обозначение=ВИРС-М-80-Ф-25-55-232-2100-100; Потребляемая мощность=5 Вт; Радиус условный=40 мм; Радиус фланца=98 мм; Серия=2100; Степень защиты=IP55; Строительная высота=260 мм; Строительная длина=250 мм; Тип, марка=ВИРС-М-80-Ф-25-55-232-2100-100; Толщина зеркала=3 мм; Толщина фланца=21 мм
- Счётчик-расходомер электромагнитный (фланцевый) ВИРС-М DN80, PN25, серия 2300: DN=80 мм; Высота основания привода=123 мм; Высота с приводом=163 мм; Выходной сигнал=частотный; Диаметр зеркала=139 мм; Диаметр зеркала_2=65 мм; Диаметр корпуса=155 мм; Диаметр патрубка=100 мм; Диаметр условный DN=80 мм; Диаметр фланца=195 мм; Длина корпуса=152 мм; Длина по фланцам=220 мм; Исполнение=6; Класс точности=0.5; Максимальная температура среды=90 °C; Максимальный расход=160.0 м³/ч; Масса=14.00 kg; Минимальный расход=1.6 м³/ч; Обозначение=ВИРС-М-80-Ф-25-57-232-2300-050; Потребляемая мощность=5 Вт; Радиус условный=40 мм; Радиус фланца=98 мм; Серия=2300; Степень защиты=IP57; Строительная высота=260 мм; Строительная длина=250 мм; Тип, марка=ВИРС-М-80-Ф-25-57-232-2300-050; Толщина зеркала=3 мм; Толщина фланца=21 мм
- Счётчик-расходомер электромагнитный (фланцевый) ВИРС-М DN80, PN25, серия 2500: DN=80 мм; Высота основания привода=123 мм; Высота с приводом=163 мм; Выходной сигнал=частотный; Диаметр зеркала=139 мм; Диаметр зеркала_2=65 мм; Диаметр корпуса=155 мм; Диаметр патрубка=100 мм; Диаметр условный DN=80 мм; Диаметр фланца=195 мм; Длина корпуса=152 мм; Длина по фланцам=220 мм; Исполнение=8; Класс точности=0.25; Максимальная температура среды=90 °C; Максимальный расход=160.0 м³/ч; Масса=14.00 kg; Минимальный расход=6.4 м³/ч; Обозначение=ВИРС-М-80-Ф-25-57-232-2500-025; Потребляемая мощность=7 Вт; Радиус условный=40 мм; Радиус фланца=98 мм; Серия=2500; Степень защиты=IP57; Строительная высота=260 мм; Строительная длина=250 мм; Тип, марка=ВИРС-М-80-Ф-25-57-232-2500-025; Толщина зеркала=3 мм; Толщина фланца=21 мм
- Счётчик-расходомер электромагнитный (фланцевый) ВИРС-М DN100, PN25, серия 1000: DN=100 мм; Высота основания привода=123 мм; Высота с приводом=163 мм; Выходной сигнал=числоимпульсный; Диаметр зеркала=162 мм; Диаметр зеркала_2=76 мм; Диаметр корпуса=175 мм; Диаметр патрубка=120 мм; Диаметр условный DN=100 мм; Диаметр фланца=215 мм; Длина корпуса=148 мм; Длина по фланцам=220 мм; Исполнение=1; Класс точности=2; Максимальная температура среды=150 °C; Максимальный расход=200.0 м³/ч; Масса=18.00 kg; Минимальный расход=0.4 м³/ч; Обозначение=ВИРС-М-100-Ф-25-55-232-1000-200; Потребляемая мощность=5 Вт; Радиус условный=50 мм; Радиус фланца=108 мм; Серия=1000; Степень защиты=IP55; Строительная высота=270 мм; Строительная длина=250 мм; Тип, марка=ВИРС-М-100-Ф-25-55-232-1000-200; Толщина зеркала=3 мм; Толщина фланца=23 мм
- Счётчик-расходомер электромагнитный (фланцевый) ВИРС-М DN100, PN25, серия 1100: DN=100 мм; Высота основания привода=123 мм; Высота с приводом=163 мм; Выходной сигнал=числоимпульсный; Диаметр зеркала=162 мм; Диаметр зеркала_2=76 мм; Диаметр корпуса=175 мм; Диаметр патрубка=120 мм; Диаметр условный DN=100 мм; Диаметр фланца=215 мм; Длина корпуса=148 мм; Длина по фланцам=220 мм; Исполнение=3; Класс точности=1; Максимальная температура среды=150 °C; Максимальный расход=200.0 м³/ч; Масса=18.00 kg; Минимальный расход=0.8 м³/ч; Обозначение=ВИРС-М-100-Ф-25-55-232-1100-100; Потребляемая мощность=5 Вт; Радиус условный=50 мм; Радиус фланца=108 мм; Серия=1100; Степень защиты=IP55; Строительная высота=270 мм; Строительная длина=250 мм; Тип, марка=ВИРС-М-100-Ф-25-55-232-1100-100; Толщина зеркала=3 мм; Толщина фланца=23 мм
- Счётчик-расходомер электромагнитный (фланцевый) ВИРС-М DN100, PN25, серия 1300: DN=100 мм; Высота основания привода=123 мм; Высота с приводом=163 мм; Выходной сигнал=частотный; Диаметр зеркала=162 мм; Диаметр зеркала_2=76 мм; Диаметр корпуса=175 мм; Диаметр патрубка=120 мм; Диаметр условный DN=100 мм; Диаметр фланца=215 мм; Длина корпуса=148 мм; Длина по фланцам=220 мм; Исполнение=5; Класс точности=0.5; Максимальная температура среды=90 °C; Максимальный расход=200.0 м³/ч; Масса=18.00 kg; Минимальный расход=2.0 м³/ч; Обозначение=ВИРС-М-100-Ф-25-57-232-1300-050; Потребляемая мощность=5 Вт; Радиус условный=50 мм; Радиус фланца=108 мм; Серия=1300; Степень защиты=IP57; Строительная высота=270 мм; Строительная длина=250 мм; Тип, марка=ВИРС-М-100-Ф-25-57-232-1300-050; Толщина зеркала=3 мм; Толщина фланца=23 мм
- Счётчик-расходомер электромагнитный (фланцевый) ВИРС-М DN100, PN25, серия 1500: DN=100 мм; Высота основания привода=123 мм; Высота с приводом=163 мм; Выходной сигнал=частотный; Диаметр зеркала=162 мм; Диаметр зеркала_2=76 мм; Диаметр корпуса=175 мм; Диаметр патрубка=120 мм; Диаметр условный DN=100 мм; Диаметр фланца=215 мм; Длина корпуса=148 мм; Длина по фланцам=220 мм; Исполнение=7; Класс точности=0.25; Максимальная температура среды=90 °C; Максимальный расход=200.0 м³/ч; Масса=18.00 kg; Минимальный расход=8.0 м³/ч; Обозначение=ВИРС-М-100-Ф-25-57-232-1500-025; Потребляемая мощность=7 Вт; Радиус условный=50 мм; Радиус фланца=108 мм; Серия=1500; Степень защиты=IP57; Строительная высота=270 мм; Строительная длина=250 мм; Тип, марка=ВИРС-М-100-Ф-25-57-232-1500-025; Толщина зеркала=3 мм; Толщина фланца=23 мм
- Счётчик-расходомер электромагнитный (фланцевый) ВИРС-М DN100, PN25, серия 2000: DN=100 мм; Высота основания привода=123 мм; Высота с приводом=163 мм; Выходной сигнал=числоимпульсный; Диаметр зеркала=162 мм; Диаметр зеркала_2=76 мм; Диаметр корпуса=175 мм; Диаметр патрубка=120 мм; Диаметр условный DN=100 мм; Диаметр фланца=215 мм; Длина корпуса=148 мм; Длина по фланцам=220 мм; Исполнение=2; Класс точности=2; Максимальная температура среды=150 °C; Максимальный расход=250.0 м³/ч; Масса=18.00 kg; Минимальный расход=0.5 м³/ч; Обозначение=ВИРС-М-100-Ф-25-55-232-2000-200; Потребляемая мощность=5 Вт; Радиус условный=50 мм; Радиус фланца=108 мм; Серия=2000; Степень защиты=IP55; Строительная высота=270 мм; Строительная длина=250 мм; Тип, марка=ВИРС-М-100-Ф-25-55-232-2000-200; Толщина зеркала=3 мм; Толщина фланца=23 мм
- Счётчик-расходомер электромагнитный (фланцевый) ВИРС-М DN100, PN25, серия 2100: DN=100 мм; Высота основания привода=123 мм; Высота с приводом=163 мм; Выходной сигнал=числоимпульсный; Диаметр зеркала=162 мм; Диаметр зеркала_2=76 мм; Диаметр корпуса=175 мм; Диаметр патрубка=120 мм; Диаметр условный DN=100 мм; Диаметр фланца=215 мм; Длина корпуса=148 мм; Длина по фланцам=220 мм; Исполнение=4; Класс точности=1; Максимальная температура среды=150 °C; Максимальный расход=250.0 м³/ч; Масса=18.00 kg; Минимальный расход=1.0 м³/ч; Обозначение=ВИРС-М-100-Ф-25-55-232-2100-100; Потребляемая мощность=5 Вт; Радиус условный=50 мм; Радиус фланца=108 мм; Серия=2100; Степень защиты=IP55; Строительная высота=270 мм; Строительная длина=250 мм; Тип, марка=ВИРС-М-100-Ф-25-55-232-2100-100; Толщина зеркала=3 мм; Толщина фланца=23 мм
- Счётчик-расходомер электромагнитный (фланцевый) ВИРС-М DN100, PN25, серия 2300: DN=100 мм; Высота основания привода=123 мм; Высота с приводом=163 мм; Выходной сигнал=частотный; Диаметр зеркала=162 мм; Диаметр зеркала_2=76 мм; Диаметр корпуса=175 мм; Диаметр патрубка=120 мм; Диаметр условный DN=100 мм; Диаметр фланца=215 мм; Длина корпуса=148 мм; Длина по фланцам=220 мм; Исполнение=6; Класс точности=0.5; Максимальная температура среды=90 °C; Максимальный расход=250.0 м³/ч; Масса=18.00 kg; Минимальный расход=2.5 м³/ч; Обозначение=ВИРС-М-100-Ф-25-57-232-2300-050; Потребляемая мощность=5 Вт; Радиус условный=50 мм; Радиус фланца=108 мм; Серия=2300; Степень защиты=IP57; Строительная высота=270 мм; Строительная длина=250 мм; Тип, марка=ВИРС-М-100-Ф-25-57-232-2300-050; Толщина зеркала=3 мм; Толщина фланца=23 мм
- Счётчик-расходомер электромагнитный (фланцевый) ВИРС-М DN100, PN25, серия 2500: DN=100 мм; Высота основания привода=123 мм; Высота с приводом=163 мм; Выходной сигнал=частотный; Диаметр зеркала=162 мм; Диаметр зеркала_2=76 мм; Диаметр корпуса=175 мм; Диаметр патрубка=120 мм; Диаметр условный DN=100 мм; Диаметр фланца=215 мм; Длина корпуса=148 мм; Длина по фланцам=220 мм; Исполнение=8; Класс точности=0.25; Максимальная температура среды=90 °C; Максимальный расход=250.0 м³/ч; Масса=18.00 kg; Минимальный расход=10.0 м³/ч; Обозначение=ВИРС-М-100-Ф-25-57-232-2500-025; Потребляемая мощность=7 Вт; Радиус условный=50 мм; Радиус фланца=108 мм; Серия=2500; Степень защиты=IP57; Строительная высота=270 мм; Строительная длина=250 мм; Тип, марка=ВИРС-М-100-Ф-25-57-232-2500-025; Толщина зеркала=3 мм; Толщина фланца=23 мм
- Счётчик-расходомер электромагнитный (фланцевый) ВИРС-М DN150, PN25, серия 1000: DN=150 мм; Высота основания привода=195 мм; Высота с приводом=235 мм; Выходной сигнал=числоимпульсный; Диаметр зеркала=218 мм; Диаметр зеркала_2=104 мм; Диаметр корпуса=240 мм; Диаметр патрубка=170 мм; Диаметр условный DN=150 мм; Диаметр фланца=280 мм; Длина корпуса=194 мм; Длина по фланцам=270 мм; Исполнение=1; Класс точности=2; Максимальная температура среды=150 °C; Максимальный расход=312.5 м³/ч; Масса=31.00 kg; Минимальный расход=0.6 м³/ч; Обозначение=ВИРС-М-150-Ф-25-55-232-1000-200; Потребляемая мощность=5 Вт; Радиус условный=75 мм; Радиус фланца=140 мм; Серия=1000; Степень защиты=IP55; Строительная высота=375 мм; Строительная длина=300 мм; Тип, марка=ВИРС-М-150-Ф-25-55-232-1000-200; Толщина зеркала=3 мм; Толщина фланца=25 мм
- Счётчик-расходомер электромагнитный (фланцевый) ВИРС-М DN150, PN25, серия 1100: DN=150 мм; Высота основания привода=195 мм; Высота с приводом=235 мм; Выходной сигнал=числоимпульсный; Диаметр зеркала=218 мм; Диаметр зеркала_2=104 мм; Диаметр корпуса=240 мм; Диаметр патрубка=170 мм; Диаметр условный DN=150 мм; Диаметр фланца=280 мм; Длина корпуса=194 мм; Длина по фланцам=270 мм; Исполнение=3; Класс точности=1; Максимальная температура среды=150 °C; Максимальный расход=312.5 м³/ч; Масса=31.00 kg; Минимальный расход=1.3 м³/ч; Обозначение=ВИРС-М-150-Ф-25-55-232-1100-100; Потребляемая мощность=5 Вт; Радиус условный=75 мм; Радиус фланца=140 мм; Серия=1100; Степень защиты=IP55; Строительная высота=375 мм; Строительная длина=300 мм; Тип, марка=ВИРС-М-150-Ф-25-55-232-1100-100; Толщина зеркала=3 мм; Толщина фланца=25 мм
- Счётчик-расходомер электромагнитный (фланцевый) ВИРС-М DN150, PN25, серия 1300: DN=150 мм; Высота основания привода=195 мм; Высота с приводом=235 мм; Выходной сигнал=частотный; Диаметр зеркала=218 мм; Диаметр зеркала_2=104 мм; Диаметр корпуса=240 мм; Диаметр патрубка=170 мм; Диаметр условный DN=150 мм; Диаметр фланца=280 мм; Длина корпуса=194 мм; Длина по фланцам=270 мм; Исполнение=5; Класс точности=0.5; Максимальная температура среды=90 °C; Максимальный расход=312.5 м³/ч; Масса=31.00 kg; Минимальный расход=3.1 м³/ч; Обозначение=ВИРС-М-150-Ф-25-57-232-1300-050; Потребляемая мощность=5 Вт; Радиус условный=75 мм; Радиус фланца=140 мм; Серия=1300; Степень защиты=IP57; Строительная высота=375 мм; Строительная длина=300 мм; Тип, марка=ВИРС-М-150-Ф-25-57-232-1300-050; Толщина зеркала=3 мм; Толщина фланца=25 мм
- Счётчик-расходомер электромагнитный (фланцевый) ВИРС-М DN150, PN25, серия 1500: DN=150 мм; Высота основания привода=195 мм; Высота с приводом=235 мм; Выходной сигнал=частотный; Диаметр зеркала=218 мм; Диаметр зеркала_2=104 мм; Диаметр корпуса=240 мм; Диаметр патрубка=170 мм; Диаметр условный DN=150 мм; Диаметр фланца=280 мм; Длина корпуса=194 мм; Длина по фланцам=270 мм; Исполнение=7; Класс точности=0.25; Максимальная температура среды=90 °C; Максимальный расход=312.5 м³/ч; Масса=31.00 kg; Минимальный расход=13.0 м³/ч; Обозначение=ВИРС-М-150-Ф-25-57-232-1500-025; Потребляемая мощность=7 Вт; Радиус условный=75 мм; Радиус фланца=140 мм; Серия=1500; Степень защиты=IP57; Строительная высота=375 мм; Строительная длина=300 мм; Тип, марка=ВИРС-М-150-Ф-25-57-232-1500-025; Толщина зеркала=3 мм; Толщина фланца=25 мм
- Счётчик-расходомер электромагнитный (фланцевый) ВИРС-М DN150, PN25, серия 2000: DN=150 мм; Высота основания привода=195 мм; Высота с приводом=235 мм; Выходной сигнал=числоимпульсный; Диаметр зеркала=218 мм; Диаметр зеркала_2=104 мм; Диаметр корпуса=240 мм; Диаметр патрубка=170 мм; Диаметр условный DN=150 мм; Диаметр фланца=280 мм; Длина корпуса=194 мм; Длина по фланцам=270 мм; Исполнение=2; Класс точности=2; Максимальная температура среды=150 °C; Максимальный расход=400.0 м³/ч; Масса=31.00 kg; Минимальный расход=0.8 м³/ч; Обозначение=ВИРС-М-150-Ф-25-55-232-2000-200; Потребляемая мощность=5 Вт; Радиус условный=75 мм; Радиус фланца=140 мм; Серия=2000; Степень защиты=IP55; Строительная высота=375 мм; Строительная длина=300 мм; Тип, марка=ВИРС-М-150-Ф-25-55-232-2000-200; Толщина зеркала=3 мм; Толщина фланца=25 мм
- Счётчик-расходомер электромагнитный (фланцевый) ВИРС-М DN150, PN25, серия 2100: DN=150 мм; Высота основания привода=195 мм; Высота с приводом=235 мм; Выходной сигнал=числоимпульсный; Диаметр зеркала=218 мм; Диаметр зеркала_2=104 мм; Диаметр корпуса=240 мм; Диаметр патрубка=170 мм; Диаметр условный DN=150 мм; Диаметр фланца=280 мм; Длина корпуса=194 мм; Длина по фланцам=270 мм; Исполнение=4; Класс точности=1; Максимальная температура среды=150 °C; Максимальный расход=400.0 м³/ч; Масса=31.00 kg; Минимальный расход=1.6 м³/ч; Обозначение=ВИРС-М-150-Ф-25-55-232-2100-100; Потребляемая мощность=5 Вт; Радиус условный=75 мм; Радиус фланца=140 мм; Серия=2100; Степень защиты=IP55; Строительная высота=375 мм; Строительная длина=300 мм; Тип, марка=ВИРС-М-150-Ф-25-55-232-2100-100; Толщина зеркала=3 мм; Толщина фланца=25 мм
- Счётчик-расходомер электромагнитный (фланцевый) ВИРС-М DN150, PN25, серия 2300: DN=150 мм; Высота основания привода=195 мм; Высота с приводом=235 мм; Выходной сигнал=частотный; Диаметр зеркала=218 мм; Диаметр зеркала_2=104 мм; Диаметр корпуса=240 мм; Диаметр патрубка=170 мм; Диаметр условный DN=150 мм; Диаметр фланца=280 мм; Длина корпуса=194 мм; Длина по фланцам=270 мм; Исполнение=6; Класс точности=0.5; Максимальная температура среды=90 °C; Максимальный расход=400.0 м³/ч; Масса=31.00 kg; Минимальный расход=4.0 м³/ч; Обозначение=ВИРС-М-150-Ф-25-57-232-2300-050; Потребляемая мощность=5 Вт; Радиус условный=75 мм; Радиус фланца=140 мм; Серия=2300; Степень защиты=IP57; Строительная высота=375 мм; Строительная длина=300 мм; Тип, марка=ВИРС-М-150-Ф-25-57-232-2300-050; Толщина зеркала=3 мм; Толщина фланца=25 мм
- Счётчик-расходомер электромагнитный (фланцевый) ВИРС-М DN150, PN25, серия 2500: DN=150 мм; Высота основания привода=195 мм; Высота с приводом=235 мм; Выходной сигнал=частотный; Диаметр зеркала=218 мм; Диаметр зеркала_2=104 мм; Диаметр корпуса=240 мм; Диаметр патрубка=170 мм; Диаметр условный DN=150 мм; Диаметр фланца=280 мм; Длина корпуса=194 мм; Длина по фланцам=270 мм; Исполнение=8; Класс точности=0.25; Максимальная температура среды=90 °C; Максимальный расход=400.0 м³/ч; Масса=31.00 kg; Минимальный расход=16.0 м³/ч; Обозначение=ВИРС-М-150-Ф-25-57-232-2500-025; Потребляемая мощность=7 Вт; Радиус условный=75 мм; Радиус фланца=140 мм; Серия=2500; Степень защиты=IP57; Строительная высота=375 мм; Строительная длина=300 мм; Тип, марка=ВИРС-М-150-Ф-25-57-232-2500-025; Толщина зеркала=3 мм; Толщина фланца=25 мм
- Счётчик-расходомер электромагнитный (фланцевый) ВИРС-М DN200, PN25, серия 1000: DN=200 мм; Высота основания привода=168 мм; Высота с приводом=208 мм; Выходной сигнал=числоимпульсный; Диаметр зеркала=274 мм; Диаметр зеркала_2=132 мм; Диаметр корпуса=295 мм; Диаметр патрубка=220 мм; Диаметр условный DN=200 мм; Диаметр фланца=335 мм; Длина корпуса=240 мм; Длина по фланцам=320 мм; Исполнение=1; Класс точности=2; Максимальная температура среды=150 °C; Максимальный расход=500.0 м³/ч; Масса=34.00 kg; Минимальный расход=1.0 м³/ч; Обозначение=ВИРС-М-200-Ф-25-55-232-1000-200; Потребляемая мощность=5 Вт; Радиус условный=100 мм; Радиус фланца=168 мм; Серия=1000; Степень защиты=IP55; Строительная высота=375 мм; Строительная длина=350 мм; Тип, марка=ВИРС-М-200-Ф-25-55-232-1000-200; Толщина зеркала=3 мм; Толщина фланца=27 мм
- Счётчик-расходомер электромагнитный (фланцевый) ВИРС-М DN200, PN25, серия 1100: DN=200 мм; Высота основания привода=168 мм; Высота с приводом=208 мм; Выходной сигнал=числоимпульсный; Диаметр зеркала=274 мм; Диаметр зеркала_2=132 мм; Диаметр корпуса=295 мм; Диаметр патрубка=220 мм; Диаметр условный DN=200 мм; Диаметр фланца=335 мм; Длина корпуса=240 мм; Длина по фланцам=320 мм; Исполнение=3; Класс точности=1; Максимальная температура среды=150 °C; Максимальный расход=500.0 м³/ч; Масса=34.00 kg; Минимальный расход=2.0 м³/ч; Обозначение=ВИРС-М-200-Ф-25-55-232-1100-100; Потребляемая мощность=5 Вт; Радиус условный=100 мм; Радиус фланца=168 мм; Серия=1100; Степень защиты=IP55; Строительная высота=375 мм; Строительная длина=350 мм; Тип, марка=ВИРС-М-200-Ф-25-55-232-1100-100; Толщина зеркала=3 мм; Толщина фланца=27 мм
- Счётчик-расходомер электромагнитный (фланцевый) ВИРС-М DN200, PN25, серия 1300: DN=200 мм; Высота основания привода=168 мм; Высота с приводом=208 мм; Выходной сигнал=частотный; Диаметр зеркала=274 мм; Диаметр зеркала_2=132 мм; Диаметр корпуса=295 мм; Диаметр патрубка=220 мм; Диаметр условный DN=200 мм; Диаметр фланца=335 мм; Длина корпуса=240 мм; Длина по фланцам=320 мм; Исполнение=5; Класс точности=0.5; Максимальная температура среды=90 °C; Максимальный расход=500.0 м³/ч; Масса=34.00 kg; Минимальный расход=5.0 м³/ч; Обозначение=ВИРС-М-200-Ф-25-57-232-1300-050; Потребляемая мощность=5 Вт; Радиус условный=100 мм; Радиус фланца=168 мм; Серия=1300; Степень защиты=IP57; Строительная высота=375 мм; Строительная длина=350 мм; Тип, марка=ВИРС-М-200-Ф-25-57-232-1300-050; Толщина зеркала=3 мм; Толщина фланца=27 мм
- Счётчик-расходомер электромагнитный (фланцевый) ВИРС-М DN200, PN25, серия 1500: DN=200 мм; Высота основания привода=168 мм; Высота с приводом=208 мм; Выходной сигнал=частотный; Диаметр зеркала=274 мм; Диаметр зеркала_2=132 мм; Диаметр корпуса=295 мм; Диаметр патрубка=220 мм; Диаметр условный DN=200 мм; Диаметр фланца=335 мм; Длина корпуса=240 мм; Длина по фланцам=320 мм; Исполнение=7; Класс точности=0.25; Максимальная температура среды=90 °C; Максимальный расход=500.0 м³/ч; Масса=34.00 kg; Минимальный расход=20.0 м³/ч; Обозначение=ВИРС-М-200-Ф-25-57-232-1500-025; Потребляемая мощность=7 Вт; Радиус условный=100 мм; Радиус фланца=168 мм; Серия=1500; Степень защиты=IP57; Строительная высота=375 мм; Строительная длина=350 мм; Тип, марка=ВИРС-М-200-Ф-25-57-232-1500-025; Толщина зеркала=3 мм; Толщина фланца=27 мм
- Счётчик-расходомер электромагнитный (фланцевый) ВИРС-М DN200, PN25, серия 2000: DN=200 мм; Высота основания привода=168 мм; Высота с приводом=208 мм; Выходной сигнал=числоимпульсный; Диаметр зеркала=274 мм; Диаметр зеркала_2=132 мм; Диаметр корпуса=295 мм; Диаметр патрубка=220 мм; Диаметр условный DN=200 мм; Диаметр фланца=335 мм; Длина корпуса=240 мм; Длина по фланцам=320 мм; Исполнение=2; Класс точности=2; Максимальная температура среды=150 °C; Максимальный расход=630.0 м³/ч; Масса=34.00 kg; Минимальный расход=1.3 м³/ч; Обозначение=ВИРС-М-200-Ф-25-55-232-2000-200; Потребляемая мощность=5 Вт; Радиус условный=100 мм; Радиус фланца=168 мм; Серия=2000; Степень защиты=IP55; Строительная высота=375 мм; Строительная длина=350 мм; Тип, марка=ВИРС-М-200-Ф-25-55-232-2000-200; Толщина зеркала=3 мм; Толщина фланца=27 мм
- Счётчик-расходомер электромагнитный (фланцевый) ВИРС-М DN200, PN25, серия 2100: DN=200 мм; Высота основания привода=168 мм; Высота с приводом=208 мм; Выходной сигнал=числоимпульсный; Диаметр зеркала=274 мм; Диаметр зеркала_2=132 мм; Диаметр корпуса=295 мм; Диаметр патрубка=220 мм; Диаметр условный DN=200 мм; Диаметр фланца=335 мм; Длина корпуса=240 мм; Длина по фланцам=320 мм; Исполнение=4; Класс точности=1; Максимальная температура среды=150 °C; Максимальный расход=630.0 м³/ч; Масса=34.00 kg; Минимальный расход=2.5 м³/ч; Обозначение=ВИРС-М-200-Ф-25-55-232-2100-100; Потребляемая мощность=5 Вт; Радиус условный=100 мм; Радиус фланца=168 мм; Серия=2100; Степень защиты=IP55; Строительная высота=375 мм; Строительная длина=350 мм; Тип, марка=ВИРС-М-200-Ф-25-55-232-2100-100; Толщина зеркала=3 мм; Толщина фланца=27 мм
- Счётчик-расходомер электромагнитный (фланцевый) ВИРС-М DN200, PN25, серия 2300: DN=200 мм; Высота основания привода=168 мм; Высота с приводом=208 мм; Выходной сигнал=частотный; Диаметр зеркала=274 мм; Диаметр зеркала_2=132 мм; Диаметр корпуса=295 мм; Диаметр патрубка=220 мм; Диаметр условный DN=200 мм; Диаметр фланца=335 мм; Длина корпуса=240 мм; Длина по фланцам=320 мм; Исполнение=6; Класс точности=0.5; Максимальная температура среды=90 °C; Максимальный расход=630.0 м³/ч; Масса=34.00 kg; Минимальный расход=6.3 м³/ч; Обозначение=ВИРС-М-200-Ф-25-57-232-2300-050; Потребляемая мощность=5 Вт; Радиус условный=100 мм; Радиус фланца=168 мм; Серия=2300; Степень защиты=IP57; Строительная высота=375 мм; Строительная длина=350 мм; Тип, марка=ВИРС-М-200-Ф-25-57-232-2300-050; Толщина зеркала=3 мм; Толщина фланца=27 мм
- Счётчик-расходомер электромагнитный (фланцевый) ВИРС-М DN200, PN25, серия 2500: DN=200 мм; Высота основания привода=168 мм; Высота с приводом=208 мм; Выходной сигнал=частотный; Диаметр зеркала=274 мм; Диаметр зеркала_2=132 мм; Диаметр корпуса=295 мм; Диаметр патрубка=220 мм; Диаметр условный DN=200 мм; Диаметр фланца=335 мм; Длина корпуса=240 мм; Длина по фланцам=320 мм; Исполнение=8; Класс точности=0.25; Максимальная температура среды=90 °C; Максимальный расход=630.0 м³/ч; Масса=34.00 kg; Минимальный расход=25.0 м³/ч; Обозначение=ВИРС-М-200-Ф-25-57-232-2500-025; Потребляемая мощность=7 Вт; Радиус условный=100 мм; Радиус фланца=168 мм; Серия=2500; Степень защиты=IP57; Строительная высота=375 мм; Строительная длина=350 мм; Тип, марка=ВИРС-М-200-Ф-25-57-232-2500-025; Толщина зеркала=3 мм; Толщина фланца=27 мм
